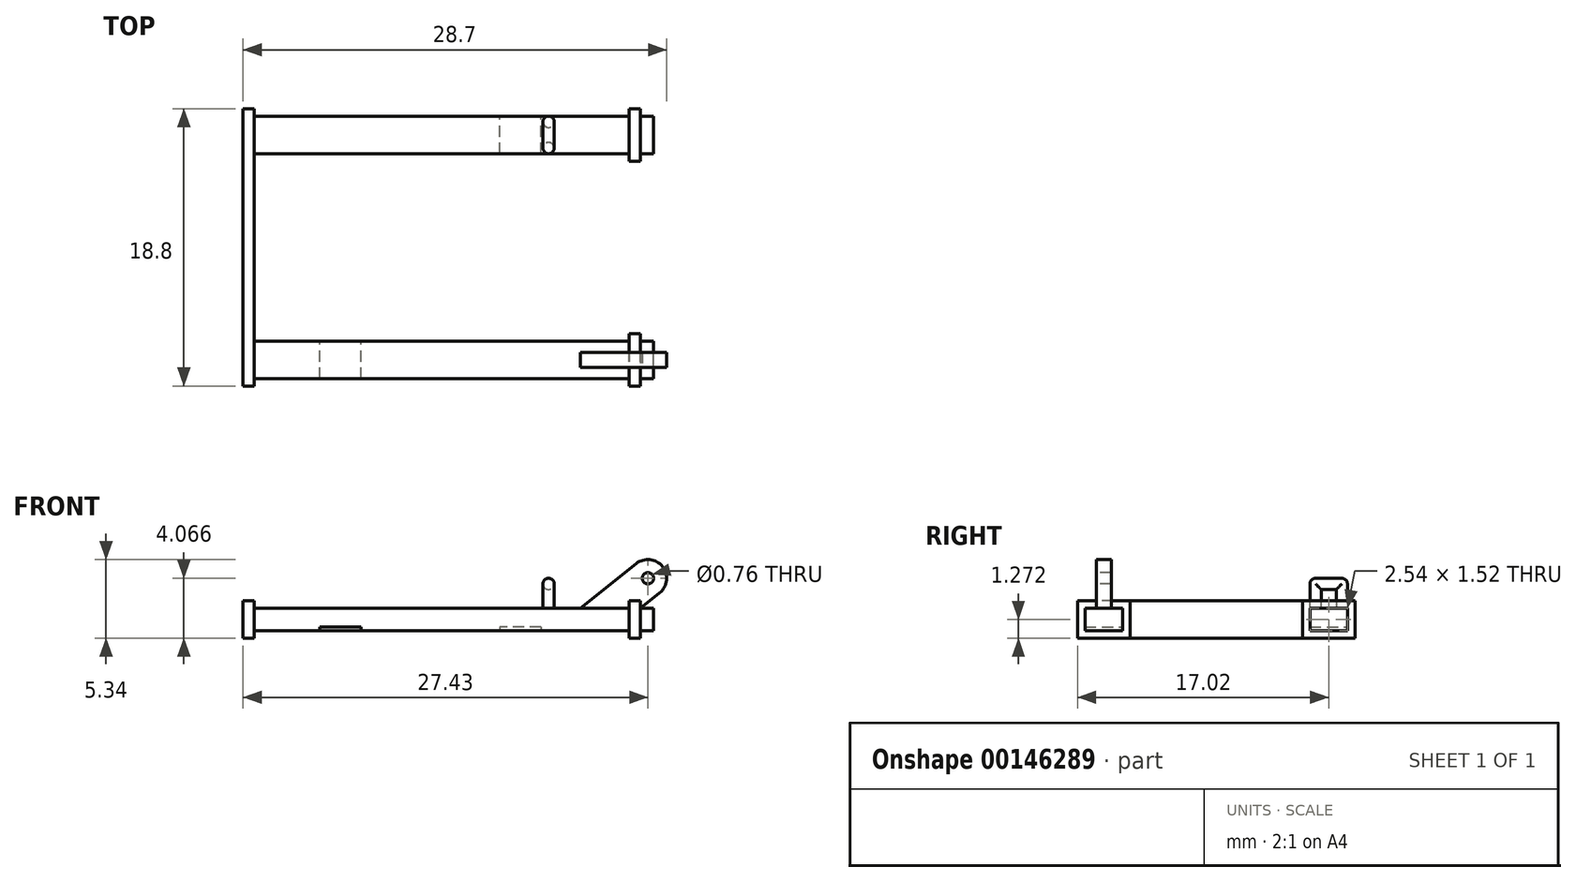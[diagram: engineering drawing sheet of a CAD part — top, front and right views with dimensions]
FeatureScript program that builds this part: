
annotation { "Feature Type Name" : "Feature", "Feature Type Description" : "" }
export const myFeature = defineFeature(function(context is Context, id is Id, definition is map)
    precondition{}
    {
        {
            var Q0;
            Q0=qCreatedBy(makeId("Top.planeOp"),FACE);
            var sketch = newSketch(context, id + "F0", { "sketchPlane" : qUnion([Q0])});
            skLineSegment(sketch, "E0.bottom", {"start": v(-12.7, 2.54) * mm, "end": v(12.7, 2.54) * mm});
            skLineSegment(sketch, "E0.top", {"start": v(-12.7, 0) * mm, "end": v(12.7, 0) * mm});
            skLineSegment(sketch, "E0.left", {"start": v(-12.7, 2.54) * mm, "end": v(-12.7, 0) * mm});
            skLineSegment(sketch, "E0.right", {"start": v(12.7, 2.54) * mm, "end": v(12.7, 0) * mm});
            skLineSegment(sketch, "E1.bottom", {"start": v(-12.7, 15.24) * mm, "end": v(12.7, 15.24) * mm});
            skLineSegment(sketch, "E1.top", {"start": v(-12.7, 17.78) * mm, "end": v(12.7, 17.78) * mm});
            skLineSegment(sketch, "E1.left", {"start": v(-12.7, 15.24) * mm, "end": v(-12.7, 17.78) * mm});
            skLineSegment(sketch, "E1.right", {"start": v(12.7, 15.24) * mm, "end": v(12.7, 17.78) * mm});
            skLineSegment(sketch, "E2.bottom", {"start": v(12.7, 18.29) * mm, "end": v(13.46, 18.29) * mm});
            skLineSegment(sketch, "E2.top", {"start": v(12.7, 14.73) * mm, "end": v(13.46, 14.73) * mm});
            skLineSegment(sketch, "E2.left", {"start": v(12.7, 18.29) * mm, "end": v(12.7, 14.73) * mm});
            skLineSegment(sketch, "E2.right", {"start": v(13.46, 18.29) * mm, "end": v(13.46, 14.73) * mm});
            skLineSegment(sketch, "E3.bottom", {"start": v(12.7, 3.05) * mm, "end": v(13.46, 3.05) * mm});
            skLineSegment(sketch, "E3.top", {"start": v(12.7, -0.5) * mm, "end": v(13.46, -0.5) * mm});
            skLineSegment(sketch, "E3.left", {"start": v(12.7, 3.05) * mm, "end": v(12.7, -0.5) * mm});
            skLineSegment(sketch, "E3.right", {"start": v(13.46, 3.05) * mm, "end": v(13.46, -0.5) * mm});
            skLineSegment(sketch, "E4.bottom", {"start": v(-12.7, 18.29) * mm, "end": v(-13.46, 18.29) * mm});
            skLineSegment(sketch, "E4.top", {"start": v(-12.7, -0.5) * mm, "end": v(-13.46, -0.5) * mm});
            skLineSegment(sketch, "E4.left", {"start": v(-12.7, 18.29) * mm, "end": v(-12.7, -0.5) * mm});
            skLineSegment(sketch, "E4.right", {"start": v(-13.46, 18.29) * mm, "end": v(-13.46, -0.5) * mm});
            skLineSegment(sketch, "E5.bottom", {"start": v(7.62, 15.24) * mm, "end": v(9.14, 15.24) * mm});
            skLineSegment(sketch, "E5.top", {"start": v(7.62, 2.54) * mm, "end": v(9.14, 2.54) * mm});
            skLineSegment(sketch, "E5.left", {"start": v(7.62, 15.24) * mm, "end": v(7.62, 2.54) * mm});
            skLineSegment(sketch, "E5.right", {"start": v(9.14, 15.24) * mm, "end": v(9.14, 2.54) * mm});
            skSolve(sketch);
        }
        {
            var Q0;
            {var subQ3=sQuery(id+"F0.wireOp",EDGE,"E1.top");Q0=makeQuery(id+"F0.imprint","IMPRINT",FACE,{"disambiguationData":[TD([[makeQuery(id+"F0.imprint","IMPRINT",EDGE,{"derivedFrom":subQ3}),-1.0]])]});}
            var Q1;
            {var subQ3=sQuery(id+"F0.wireOp",EDGE,"E4.bottom");Q1=makeQuery(id+"F0.imprint","IMPRINT",FACE,{"disambiguationData":[TD([[makeQuery(id+"F0.imprint","IMPRINT",EDGE,{"derivedFrom":subQ3}),1.0]])]});}
            var Q2;
            {var subQ3=sQuery(id+"F0.wireOp",EDGE,"E0.top");Q2=makeQuery(id+"F0.imprint","IMPRINT",FACE,{"disambiguationData":[TD([[makeQuery(id+"F0.imprint","IMPRINT",EDGE,{"derivedFrom":subQ3}),1.0]])]});}
            var Q3;
            Q3=makeQuery(id+"F0.imprint","IMPRINT",FACE,{"disambiguationData":[TD([[makeQuery(id+"F0.imprint","IMPRINT",EDGE,{"derivedFrom":sQuery(id+"F0.wireOp",EDGE,"E5.bottom")}),-1.0]])]});
            var Q4;
            {var subQ3=sQuery(id+"F0.wireOp",EDGE,"E3.bottom");Q4=makeQuery(id+"F0.imprint","IMPRINT",FACE,{"disambiguationData":[TD([[makeQuery(id+"F0.imprint","IMPRINT",EDGE,{"derivedFrom":subQ3}),-1.0]])]});}
            var Q5;
            {var subQ3=sQuery(id+"F0.wireOp",EDGE,"E2.bottom");Q5=makeQuery(id+"F0.imprint","IMPRINT",FACE,{"disambiguationData":[TD([[makeQuery(id+"F0.imprint","IMPRINT",EDGE,{"derivedFrom":subQ3}),-1.0]])]});}
            extrude(context, id + "F1", {"entities" : qUnion([Q0, Q1, Q2, Q3, Q4, Q5]), "depth" : 1.52 * mm});
        }
        {
            var Q0;
            Q0=makeQuery(id+"F1.opExtrude","CAP_FACE",FACE,{"disambiguationData":[OSD([sQuery(id+"F0.wireOp",EDGE,"E0.bottom"),sQuery(id+"F0.wireOp",EDGE,"E0.top"),sQuery(id+"F0.wireOp",EDGE,"E1.bottom"),sQuery(id+"F0.wireOp",EDGE,"E1.top"),sQuery(id+"F0.wireOp",EDGE,"E2.bottom"),sQuery(id+"F0.wireOp",EDGE,"E2.top"),sQuery(id+"F0.wireOp",EDGE,"E2.left"),sQuery(id+"F0.wireOp",EDGE,"E2.right"),sQuery(id+"F0.wireOp",EDGE,"E3.bottom"),sQuery(id+"F0.wireOp",EDGE,"E3.top"),sQuery(id+"F0.wireOp",EDGE,"E3.left"),sQuery(id+"F0.wireOp",EDGE,"E3.right"),sQuery(id+"F0.wireOp",EDGE,"E4.bottom"),sQuery(id+"F0.wireOp",EDGE,"E4.top"),sQuery(id+"F0.wireOp",EDGE,"E4.left"),sQuery(id+"F0.wireOp",EDGE,"E4.right"),sQuery(id+"F0.wireOp",EDGE,"E5.left"),sQuery(id+"F0.wireOp",EDGE,"E5.right")])],"isStart":false});
            var sketch = newSketch(context, id + "F2", { "sketchPlane" : qUnion([Q0])});
            skLineSegment(sketch, "E6.bottom", {"start": v(-13.46, 18.29) * mm, "end": v(-12.7, 18.29) * mm});
            skLineSegment(sketch, "E6.top", {"start": v(-13.46, -0.5) * mm, "end": v(-12.7, -0.5) * mm});
            skLineSegment(sketch, "E6.left", {"start": v(-13.46, 18.29) * mm, "end": v(-13.46, -0.5) * mm});
            skLineSegment(sketch, "E6.right", {"start": v(-12.7, 18.29) * mm, "end": v(-12.7, -0.5) * mm});
            skLineSegment(sketch, "E7.bottom", {"start": v(12.7, 18.29) * mm, "end": v(13.46, 18.29) * mm});
            skLineSegment(sketch, "E7.top", {"start": v(12.7, 14.73) * mm, "end": v(13.46, 14.73) * mm});
            skLineSegment(sketch, "E7.left", {"start": v(12.7, 18.29) * mm, "end": v(12.7, 14.73) * mm});
            skLineSegment(sketch, "E7.right", {"start": v(13.46, 18.29) * mm, "end": v(13.46, 14.73) * mm});
            skLineSegment(sketch, "E8.bottom", {"start": v(12.7, 3.05) * mm, "end": v(13.46, 3.05) * mm});
            skLineSegment(sketch, "E8.top", {"start": v(12.7, -0.5) * mm, "end": v(13.46, -0.5) * mm});
            skLineSegment(sketch, "E8.left", {"start": v(12.7, 3.05) * mm, "end": v(12.7, -0.5) * mm});
            skLineSegment(sketch, "E8.right", {"start": v(13.46, 3.05) * mm, "end": v(13.46, -0.5) * mm});
            skSolve(sketch);
        }
        {
            var Q0;
            Q0 = qSketchRegion(id + "F2", true);
            extrude(context, id + "F3", {"entities" : qUnion([Q0]), "operationType" : NewBodyOperationType.ADD, "depth" : 0.5 * mm, "hasSecondDirection" : true, "secondDirectionOppositeDirection" : true, "secondDirectionDepth" : 2.03 * mm});
        }
        {
            var Q0;
            Q0=makeQuery(id+"F1.opExtrude","SWEPT_FACE",FACE,{"disambiguationData":[OSD([sQuery(id+"F0.wireOp",EDGE,"E0.top")])]});
            var sketch = newSketch(context, id + "F4", { "sketchPlane" : qUnion([Q0])});
            skLineSegment(sketch, "E9", {"start": v(14.76, 2.56) * mm, "end": v(13.46, 1.52) * mm});
            skArc(sketch, "E10", {"start": v(14.76, 2.56) * mm, "mid": v(14.96, 4.35) * mm, "end": v(13.18, 4.55) * mm});
            skLineSegment(sketch, "E11", {"start": v(13.18, 4.55) * mm, "end": v(9.4, 1.52) * mm});
            skLineSegment(sketch, "E12", {"start": v(9.4, 1.52) * mm, "end": v(13.46, 1.52) * mm});
            skCircle(sketch, "E13", {"center": v(13.97, 3.56) * mm, "radius": 0.38 * mm});
            skSolve(sketch);
        }
        {
            var Q0;
            Q0 = qSketchRegion(id + "F4", true);
            extrude(context, id + "F5", {"entities" : qUnion([Q0]), "operationType" : NewBodyOperationType.ADD, "oppositeDirection" : true, "depth" : 1.78 * mm});
        }
        {
            var Q0;
            Q0=makeQuery(id+"F5.boolean.opBoolean","MERGE",FACE,{"derivedFrom":[makeQuery(id+"F1.opExtrude","SWEPT_FACE",FACE,{"disambiguationData":[OSD([sQuery(id+"F0.wireOp",EDGE,"E0.top")])]}),makeQuery(id+"F5.opExtrude","CAP_FACE",FACE,{"disambiguationData":[OSD([sQuery(id+"F4.wireOp",EDGE,"E9"),sQuery(id+"F4.wireOp",EDGE,"E10"),sQuery(id+"F4.wireOp",EDGE,"E11"),sQuery(id+"F4.wireOp",EDGE,"E12"),sQuery(id+"F4.wireOp",EDGE,"E13")])],"isStart":true})]});
            var sketch = newSketch(context, id + "F6", { "sketchPlane" : qUnion([Q0])});
            skLineSegment(sketch, "E14", {"start": v(9.4, 1.52) * mm, "end": v(12.7, 1.52) * mm});
            skLineSegment(sketch, "E15", {"start": v(12.7, 1.52) * mm, "end": v(12.7, 2.03) * mm});
            skLineSegment(sketch, "E16", {"start": v(12.7, 2.03) * mm, "end": v(13.46, 2.03) * mm});
            skLineSegment(sketch, "E17", {"start": v(13.46, 2.03) * mm, "end": v(13.46, 1.52) * mm});
            skLineSegment(sketch, "E18", {"start": v(13.46, 1.52) * mm, "end": v(14.76, 2.56) * mm});
            skArc(sketch, "E19", {"start": v(14.76, 2.56) * mm, "mid": v(14.96, 4.35) * mm, "end": v(13.18, 4.55) * mm});
            skLineSegment(sketch, "E20", {"start": v(9.4, 1.52) * mm, "end": v(13.18, 4.55) * mm});
            skSolve(sketch);
        }
        {
            var Q0;
            Q0 = qSketchRegion(id + "F6", true);
            extrude(context, id + "F7", {"entities" : qUnion([Q0]), "operationType" : NewBodyOperationType.REMOVE, "oppositeDirection" : true, "depth" : 0.76 * mm});
        }
        {
            var Q0;
            Q0=makeQuery(id+"F5.boolean.opBoolean","MERGE",FACE,{"derivedFrom":[makeQuery(id+"F1.opExtrude","SWEPT_FACE",FACE,{"disambiguationData":[OSD([sQuery(id+"F0.wireOp",EDGE,"E0.top")])]}),makeQuery(id+"F5.opExtrude","CAP_FACE",FACE,{"disambiguationData":[OSD([sQuery(id+"F4.wireOp",EDGE,"E9"),sQuery(id+"F4.wireOp",EDGE,"E10"),sQuery(id+"F4.wireOp",EDGE,"E11"),sQuery(id+"F4.wireOp",EDGE,"E12"),sQuery(id+"F4.wireOp",EDGE,"E13")])],"isStart":true})]});
            cPlane(context, id + "F8", {"entities" : qUnion([Q0]), "cplaneType" : CPlaneType.OFFSET, "offset" : 8.9 * mm, "oppositeDirection" : true, "width" : 152.4 * mm, "height" : 152.4 * mm});
        }
        {
            var Q0;
            Q0=makeQuery(id+"F1.opExtrude","CAP_FACE",FACE,{"disambiguationData":[OSD([sQuery(id+"F0.wireOp",EDGE,"E0.bottom"),sQuery(id+"F0.wireOp",EDGE,"E0.top"),sQuery(id+"F0.wireOp",EDGE,"E1.bottom"),sQuery(id+"F0.wireOp",EDGE,"E1.top"),sQuery(id+"F0.wireOp",EDGE,"E2.bottom"),sQuery(id+"F0.wireOp",EDGE,"E2.top"),sQuery(id+"F0.wireOp",EDGE,"E2.left"),sQuery(id+"F0.wireOp",EDGE,"E2.right"),sQuery(id+"F0.wireOp",EDGE,"E3.bottom"),sQuery(id+"F0.wireOp",EDGE,"E3.top"),sQuery(id+"F0.wireOp",EDGE,"E3.left"),sQuery(id+"F0.wireOp",EDGE,"E3.right"),sQuery(id+"F0.wireOp",EDGE,"E4.bottom"),sQuery(id+"F0.wireOp",EDGE,"E4.top"),sQuery(id+"F0.wireOp",EDGE,"E4.left"),sQuery(id+"F0.wireOp",EDGE,"E4.right"),sQuery(id+"F0.wireOp",EDGE,"E5.left"),sQuery(id+"F0.wireOp",EDGE,"E5.right")])],"isStart":true});
            var sketch = newSketch(context, id + "F9", { "sketchPlane" : qUnion([Q0])});
            skLineSegment(sketch, "E21.bottom", {"start": v(6.73, -15.24) * mm, "end": v(3.94, -15.24) * mm});
            skLineSegment(sketch, "E21.top", {"start": v(6.73, -17.78) * mm, "end": v(3.94, -17.78) * mm});
            skLineSegment(sketch, "E21.left", {"start": v(6.73, -15.24) * mm, "end": v(6.73, -17.78) * mm});
            skLineSegment(sketch, "E21.right", {"start": v(3.94, -15.24) * mm, "end": v(3.94, -17.78) * mm});
            skLineSegment(sketch, "E22.bottom", {"start": v(-8.26, 0) * mm, "end": v(-5.46, 0) * mm});
            skLineSegment(sketch, "E22.top", {"start": v(-8.26, -2.54) * mm, "end": v(-5.46, -2.54) * mm});
            skLineSegment(sketch, "E22.left", {"start": v(-8.26, 0) * mm, "end": v(-8.26, -2.54) * mm});
            skLineSegment(sketch, "E22.right", {"start": v(-5.46, 0) * mm, "end": v(-5.46, -2.54) * mm});
            skSolve(sketch);
        }
        {
            var Q0;
            Q0 = qSketchRegion(id + "F9", true);
            extrude(context, id + "F10", {"entities" : qUnion([Q0]), "operationType" : NewBodyOperationType.REMOVE, "oppositeDirection" : true, "depth" : 0.25 * mm});
        }
        {
            var Q0;
            Q0=makeQuery(id+"F7.boolean.opBoolean","MERGE",FACE,{"derivedFrom":[makeQuery(id+"F3.boolean.opBoolean","MERGE",FACE,{"derivedFrom":[makeQuery(id+"F1.opExtrude","SWEPT_FACE",FACE,{"disambiguationData":[OSD([sQuery(id+"F0.wireOp",EDGE,"E3.right")])]}),makeQuery(id+"F3.opExtrude","SWEPT_FACE",FACE,{"disambiguationData":[OSD([sQuery(id+"F2.wireOp",EDGE,"E8.right")])]})]}),makeQuery(id+"F7.opExtrude","SWEPT_FACE",FACE,{"disambiguationData":[OSD([sQuery(id+"F6.wireOp",EDGE,"E17")])]})]});
            var sketch = newSketch(context, id + "F11", { "sketchPlane" : qUnion([Q0])});
            skLineSegment(sketch, "E23.bottom", {"start": v(0, 1.52) * mm, "end": v(2.54, 1.52) * mm});
            skLineSegment(sketch, "E23.top", {"start": v(0, 0) * mm, "end": v(2.54, 0) * mm});
            skLineSegment(sketch, "E23.left", {"start": v(0, 1.52) * mm, "end": v(0, 0) * mm});
            skLineSegment(sketch, "E23.right", {"start": v(2.54, 1.52) * mm, "end": v(2.54, 0) * mm});
            skSolve(sketch);
        }
        {
            var Q0;
            Q0 = qSketchRegion(id + "F11", true);
            extrude(context, id + "F12", {"entities" : qUnion([Q0]), "operationType" : NewBodyOperationType.ADD, "depth" : 0.89 * mm});
        }
        {
            var Q0;
            Q0=makeQuery(id+"FbFiRezVOLwQmsc_1.1.F7.boolean.opBoolean","MERGE",FACE,{"derivedFrom":[makeQuery(id+"F3.boolean.opBoolean","MERGE",FACE,{"derivedFrom":[makeQuery(id+"F1.opExtrude","SWEPT_FACE",FACE,{"disambiguationData":[OSD([sQuery(id+"F0.wireOp",EDGE,"E2.right")])]}),makeQuery(id+"F3.opExtrude","SWEPT_FACE",FACE,{"disambiguationData":[OSD([sQuery(id+"F2.wireOp",EDGE,"E7.right")])]})]}),makeQuery(id+"FbFiRezVOLwQmsc_1.1.F7.opExtrude","SWEPT_FACE",FACE,{"disambiguationData":[OSD([sQuery(id+"F6.wireOp",EDGE,"E17")])]})]});
            var sketch = newSketch(context, id + "F13", { "sketchPlane" : qUnion([Q0])});
            skLineSegment(sketch, "E24.bottom", {"start": v(15.24, 1.52) * mm, "end": v(17.78, 1.52) * mm});
            skLineSegment(sketch, "E24.top", {"start": v(15.24, 0) * mm, "end": v(17.78, 0) * mm});
            skLineSegment(sketch, "E24.left", {"start": v(15.24, 1.52) * mm, "end": v(15.24, 0) * mm});
            skLineSegment(sketch, "E24.right", {"start": v(17.78, 1.52) * mm, "end": v(17.78, 0) * mm});
            skSolve(sketch);
        }
        {
            var Q0;
            Q0 = qSketchRegion(id + "F13", true);
            extrude(context, id + "F14", {"entities" : qUnion([Q0]), "operationType" : NewBodyOperationType.ADD, "depth" : 0.89 * mm});
        }
        {
            var Q0;
            {var subQ0=sQuery(id+"F6.wireOp",EDGE,"E14");Q0=makeQuery(id+"FbFiRezVOLwQmsc_1.1.F7.boolean.opBoolean","MERGE",FACE,{"derivedFrom":[makeQuery(id+"F7.boolean.opBoolean","MERGE",FACE,{"derivedFrom":[makeQuery(id+"F1.opExtrude","CAP_FACE",FACE,{"disambiguationData":[OSD([sQuery(id+"F0.wireOp",EDGE,"E0.bottom"),sQuery(id+"F0.wireOp",EDGE,"E0.top"),sQuery(id+"F0.wireOp",EDGE,"E1.bottom"),sQuery(id+"F0.wireOp",EDGE,"E1.top"),sQuery(id+"F0.wireOp",EDGE,"E2.bottom"),sQuery(id+"F0.wireOp",EDGE,"E2.top"),sQuery(id+"F0.wireOp",EDGE,"E2.left"),sQuery(id+"F0.wireOp",EDGE,"E2.right"),sQuery(id+"F0.wireOp",EDGE,"E3.bottom"),sQuery(id+"F0.wireOp",EDGE,"E3.top"),sQuery(id+"F0.wireOp",EDGE,"E3.left"),sQuery(id+"F0.wireOp",EDGE,"E3.right"),sQuery(id+"F0.wireOp",EDGE,"E4.bottom"),sQuery(id+"F0.wireOp",EDGE,"E4.top"),sQuery(id+"F0.wireOp",EDGE,"E4.left"),sQuery(id+"F0.wireOp",EDGE,"E4.right"),sQuery(id+"F0.wireOp",EDGE,"E5.left"),sQuery(id+"F0.wireOp",EDGE,"E5.right")])],"isStart":false}),makeQuery(id+"F7.opExtrude","SWEPT_FACE",FACE,{"disambiguationData":[OSD([subQ0])]})]}),makeQuery(id+"FbFiRezVOLwQmsc_1.1.F7.opExtrude","SWEPT_FACE",FACE,{"disambiguationData":[OSD([subQ0])]})]});}
            var sketch = newSketch(context, id + "F15", { "sketchPlane" : qUnion([Q0])});
            skLineSegment(sketch, "E25.bottom", {"start": v(7.62, 15.24) * mm, "end": v(6.86, 15.24) * mm});
            skLineSegment(sketch, "E25.top", {"start": v(7.62, 16) * mm, "end": v(6.86, 16) * mm});
            skLineSegment(sketch, "E25.left", {"start": v(7.62, 15.24) * mm, "end": v(7.62, 16) * mm});
            skLineSegment(sketch, "E25.right", {"start": v(6.86, 15.24) * mm, "end": v(6.86, 16) * mm});
            skLineSegment(sketch, "E26.bottom", {"start": v(7.62, 17.78) * mm, "end": v(6.86, 17.78) * mm});
            skLineSegment(sketch, "E26.top", {"start": v(7.62, 17.02) * mm, "end": v(6.86, 17.02) * mm});
            skLineSegment(sketch, "E26.left", {"start": v(7.62, 17.78) * mm, "end": v(7.62, 17.02) * mm});
            skLineSegment(sketch, "E26.right", {"start": v(6.86, 17.78) * mm, "end": v(6.86, 17.02) * mm});
            skSolve(sketch);
        }
        {
            var Q0;
            Q0 = qSketchRegion(id + "F15", true);
            extrude(context, id + "F16", {"entities" : qUnion([Q0]), "operationType" : NewBodyOperationType.ADD, "depth" : 2.03 * mm});
        }
        {
            var Q0;
            Q0=makeQuery(id+"F16.opExtrude","SWEPT_FACE",FACE,{"disambiguationData":[OSD([sQuery(id+"F15.wireOp",EDGE,"E26.top")])]});
            var sketch = newSketch(context, id + "F17", { "sketchPlane" : qUnion([Q0])});
            skLineSegment(sketch, "E27.bottom", {"start": v(6.86, 3.56) * mm, "end": v(7.62, 3.56) * mm});
            skLineSegment(sketch, "E27.top", {"start": v(6.86, 2.8) * mm, "end": v(7.62, 2.8) * mm});
            skLineSegment(sketch, "E27.left", {"start": v(6.86, 3.56) * mm, "end": v(6.86, 2.8) * mm});
            skLineSegment(sketch, "E27.right", {"start": v(7.62, 3.56) * mm, "end": v(7.62, 2.8) * mm});
            skSolve(sketch);
        }
        {
            var Q0;
            Q0 = qSketchRegion(id + "F17", true);
            var Q1;
            Q1=makeQuery(id+"F16.opExtrude","SWEPT_FACE",FACE,{"disambiguationData":[OSD([sQuery(id+"F15.wireOp",EDGE,"E25.top")])]});
            extrude(context, id + "F18", {"entities" : qUnion([Q0]), "operationType" : NewBodyOperationType.ADD, "endBound" : BoundingType.UP_TO_SURFACE, "endBoundEntityFace" : qUnion([Q1]), "depth" : 25.4 * mm});
        }
        {
            var Q0;
            Q0=makeQuery(id+"F16.opExtrude","SWEPT_EDGE",EDGE,{"disambiguationData":[OSD([sQuery(id+"F0.wireOp",EDGE,"E1.top"),sQuery(id+"F6.wireOp",EDGE,"E14"),sQuery(id+"F15.wireOp",EDGE,"E26.bottom"),sQuery(id+"F15.wireOp",EDGE,"E26.right")])]});
            var Q1;
            Q1=makeQuery(id+"F16.opExtrude","SWEPT_EDGE",EDGE,{"disambiguationData":[OSD([sQuery(id+"F0.wireOp",EDGE,"E1.top"),sQuery(id+"F6.wireOp",EDGE,"E14"),sQuery(id+"F15.wireOp",EDGE,"E26.bottom"),sQuery(id+"F15.wireOp",EDGE,"E26.left")])]});
            var Q2;
            Q2=makeQuery(id+"F16.opExtrude","CAP_EDGE",EDGE,{"disambiguationData":[OSD([sQuery(id+"F15.wireOp",EDGE,"E26.bottom")])],"isStart":false});
            var Q3;
            Q3=makeQuery(id+"F18.boolean.opBoolean","MERGE",EDGE,{"derivedFrom":[makeQuery(id+"F16.opExtrude","CAP_EDGE",EDGE,{"disambiguationData":[OSD([sQuery(id+"F15.wireOp",EDGE,"E25.right")])],"isStart":false}),makeQuery(id+"F16.opExtrude","CAP_EDGE",EDGE,{"disambiguationData":[OSD([sQuery(id+"F15.wireOp",EDGE,"E26.right")])],"isStart":false}),makeQuery(id+"F18.opExtrude","SWEPT_EDGE",EDGE,{"disambiguationData":[OSD([sQuery(id+"F17.wireOp",EDGE,"E27.bottom"),sQuery(id+"F17.wireOp",EDGE,"E27.left")])]})]});
            var Q4;
            Q4=makeQuery(id+"F18.boolean.opBoolean","MERGE",EDGE,{"derivedFrom":[makeQuery(id+"F16.opExtrude","CAP_EDGE",EDGE,{"disambiguationData":[OSD([sQuery(id+"F15.wireOp",EDGE,"E25.left")])],"isStart":false}),makeQuery(id+"F16.opExtrude","CAP_EDGE",EDGE,{"disambiguationData":[OSD([sQuery(id+"F15.wireOp",EDGE,"E26.left")])],"isStart":false}),makeQuery(id+"F18.opExtrude","SWEPT_EDGE",EDGE,{"disambiguationData":[OSD([sQuery(id+"F17.wireOp",EDGE,"E27.bottom"),sQuery(id+"F17.wireOp",EDGE,"E27.right")])]})]});
            var Q5;
            Q5=makeQuery(id+"F16.opExtrude","SWEPT_EDGE",EDGE,{"disambiguationData":[OSD([sQuery(id+"F15.wireOp",EDGE,"E26.top"),sQuery(id+"F15.wireOp",EDGE,"E26.right")])]});
            var Q6;
            Q6=makeQuery(id+"F18.opExtrude","SWEPT_EDGE",EDGE,{"disambiguationData":[OSD([sQuery(id+"F15.wireOp",EDGE,"E26.top"),sQuery(id+"F15.wireOp",EDGE,"E26.right"),sQuery(id+"F17.wireOp",EDGE,"E27.top"),sQuery(id+"F17.wireOp",EDGE,"E27.left")])]});
            var Q7;
            Q7=makeQuery(id+"F16.opExtrude","SWEPT_EDGE",EDGE,{"disambiguationData":[OSD([sQuery(id+"F15.wireOp",EDGE,"E25.top"),sQuery(id+"F15.wireOp",EDGE,"E25.right")])]});
            var Q8;
            Q8=makeQuery(id+"F16.opExtrude","SWEPT_EDGE",EDGE,{"disambiguationData":[OSD([sQuery(id+"F0.wireOp",EDGE,"E1.bottom"),sQuery(id+"F15.wireOp",EDGE,"E25.bottom"),sQuery(id+"F15.wireOp",EDGE,"E25.right")])]});
            var Q9;
            Q9=makeQuery(id+"F16.opExtrude","CAP_EDGE",EDGE,{"disambiguationData":[OSD([sQuery(id+"F15.wireOp",EDGE,"E25.bottom")])],"isStart":false});
            var Q10;
            Q10=makeQuery(id+"F16.opExtrude","SWEPT_EDGE",EDGE,{"disambiguationData":[OSD([sQuery(id+"F15.wireOp",EDGE,"E26.top"),sQuery(id+"F15.wireOp",EDGE,"E26.left")])]});
            var Q11;
            Q11=makeQuery(id+"F18.opExtrude","SWEPT_EDGE",EDGE,{"disambiguationData":[OSD([sQuery(id+"F15.wireOp",EDGE,"E26.top"),sQuery(id+"F15.wireOp",EDGE,"E26.left"),sQuery(id+"F17.wireOp",EDGE,"E27.top"),sQuery(id+"F17.wireOp",EDGE,"E27.right")])]});
            var Q12;
            Q12=makeQuery(id+"F16.opExtrude","SWEPT_EDGE",EDGE,{"disambiguationData":[OSD([sQuery(id+"F15.wireOp",EDGE,"E25.top"),sQuery(id+"F15.wireOp",EDGE,"E25.left")])]});
            var Q13;
            Q13=makeQuery(id+"F16.opExtrude","SWEPT_EDGE",EDGE,{"disambiguationData":[OSD([sQuery(id+"F0.wireOp",EDGE,"E5.left"),sQuery(id+"F15.wireOp",EDGE,"E25.bottom"),sQuery(id+"F15.wireOp",EDGE,"E25.left")])]});
            fillet(context, id + "F19", {"entities" : qUnion([Q0, Q1, Q2, Q3, Q4, Q5, Q6, Q7, Q8, Q9, Q10, Q11, Q12, Q13]), "radius" : 0.38 * mm, "tangentPropagation" : true, "allowEdgeOverflow" : false});
        }
    });
